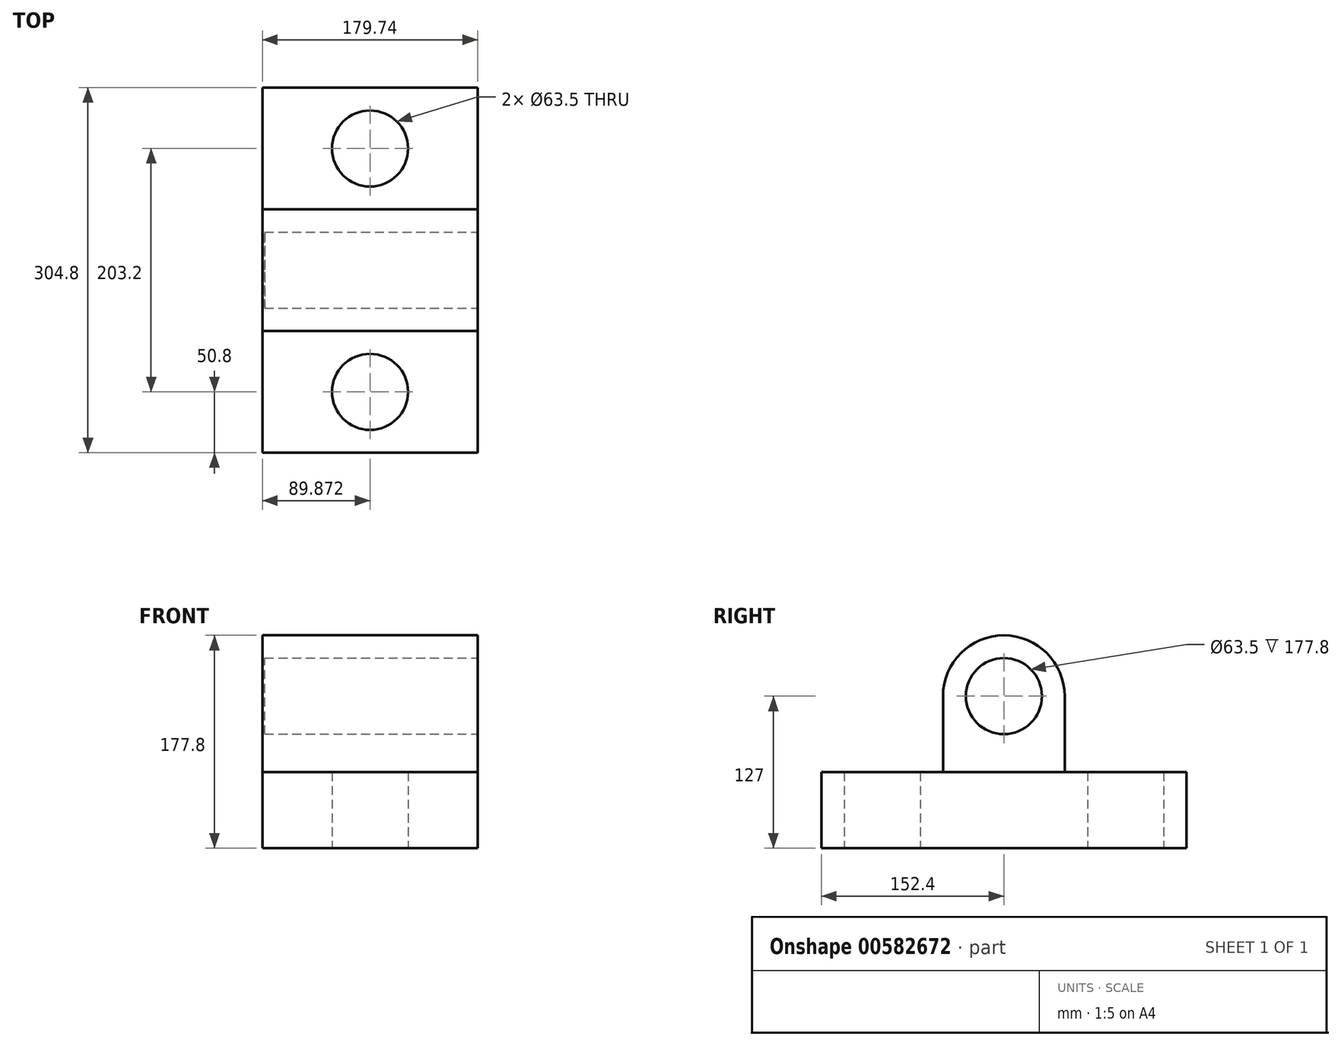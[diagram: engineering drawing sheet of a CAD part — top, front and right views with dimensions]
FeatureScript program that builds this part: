
annotation { "Feature Type Name" : "Feature", "Feature Type Description" : "" }
export const myFeature = defineFeature(function(context is Context, id is Id, definition is map)
    precondition{}
    {
        {
            var Q0;
            Q0=qCreatedBy(makeId("Top.planeOp"),FACE);
            var sketch = newSketch(context, id + "F0", { "sketchPlane" : qUnion([Q0])});
            skLineSegment(sketch, "E0.bottom", {"start": v(-43.63, 50.8) * mm, "end": v(136.11, 50.8) * mm});
            skLineSegment(sketch, "E0.top", {"start": v(-43.63, -254) * mm, "end": v(136.11, -254) * mm});
            skLineSegment(sketch, "E0.left", {"start": v(-43.63, 50.8) * mm, "end": v(-43.63, -254) * mm});
            skLineSegment(sketch, "E0.right", {"start": v(136.11, 50.8) * mm, "end": v(136.11, -254) * mm});
            skCircle(sketch, "E1", {"center": v(46.24, 0) * mm, "radius": 31.75 * mm});
            skCircle(sketch, "E2", {"center": v(46.24, -203.2) * mm, "radius": 31.75 * mm});
            skLineSegment(sketch, "E3", {"start": v(-43.63, -152.4) * mm, "end": v(136.11, -152.4) * mm});
            skPoint(sketch, "E4", {"position": v(-43.63, -50.8) * mm});
            skLineSegment(sketch, "E5", {"start": v(-43.63, -50.8) * mm, "end": v(136.11, -50.8) * mm});
            skSolve(sketch);
        }
        {
            var Q0;
            Q0 = qSketchRegion(id + "F0", true);
            extrude(context, id + "F1", {"entities" : qUnion([Q0]), "depth" : 25.4 * mm, "offsetDistance" : 25.4 * mm});
        }
        {
            var Q0;
            Q0 = qSketchRegion(id + "F0", true);
            var Q1;
            Q1=makeQuery(id+"F1.opExtrude","CAP_FACE",FACE,{"disambiguationData":[OSD([sQuery(id+"F0.wireOp",EDGE,"E0.bottom"),sQuery(id+"F0.wireOp",EDGE,"E0.top"),sQuery(id+"F0.wireOp",EDGE,"E0.left"),sQuery(id+"F0.wireOp",EDGE,"E0.right"),sQuery(id+"F0.wireOp",EDGE,"E1"),sQuery(id+"F0.wireOp",EDGE,"E2")])],"isStart":false});
            extrude(context, id + "F2", {"entities" : qUnion([Q0, Q1]), "operationType" : NewBodyOperationType.ADD, "depth" : 38.1 * mm, "offsetDistance" : 25.4 * mm});
        }
        {
            var Q0;
            {var subQ0=sQuery(id+"F0.wireOp",EDGE,"E2");var subQ1=sQuery(id+"F0.wireOp",EDGE,"E1");var subQ2=sQuery(id+"F0.wireOp",EDGE,"E0.right");var subQ3=sQuery(id+"F0.wireOp",EDGE,"E0.left");var subQ4=sQuery(id+"F0.wireOp",EDGE,"E0.top");var subQ5=sQuery(id+"F0.wireOp",EDGE,"E0.bottom");Q0=makeQuery(id+"F2.opExtrude","CAP_FACE",FACE,{"disambiguationData":[OSD([subQ5,subQ4,subQ3,subQ2,subQ1,subQ0]),TDD([makeQuery(id+"F1.opExtrude","CAP_FACE",FACE,{"disambiguationData":[OSD([subQ5,subQ4,subQ3,subQ2,subQ1,subQ0])],"isStart":false})])],"isStart":false});}
            var sketch = newSketch(context, id + "F3", { "sketchPlane" : qUnion([Q0])});
            skPoint(sketch, "E6", {"position": v(-43.63, -50.8) * mm});
            skPoint(sketch, "E7", {"position": v(-43.63, -152.4) * mm});
            skLineSegment(sketch, "E8", {"start": v(-43.63, -152.4) * mm, "end": v(136.11, -152.4) * mm});
            skLineSegment(sketch, "E9", {"start": v(-43.63, -50.8) * mm, "end": v(136.11, -50.8) * mm});
            skSolve(sketch);
        }
        {
            var Q0;
            {var subQ0=sQuery(id+"F3.wireOp",EDGE,"E8");Q0=makeQuery(id+"F3.imprint","IMPRINT",FACE,{"disambiguationData":[TD([[makeQuery(id+"F3.imprint","IMPRINT",EDGE,{"derivedFrom":subQ0}),1.0]])]});}
            extrude(context, id + "F4", {"entities" : qUnion([Q0]), "depth" : 114.3 * mm, "offsetDistance" : 25.4 * mm});
        }
        {
            var Q0;
            Q0=makeQuery(id+"F4.opExtrude","SWEPT_FACE",FACE,{"disambiguationData":[OSD([sQuery(id+"F0.wireOp",EDGE,"E0.right")])]});
            var sketch = newSketch(context, id + "F5", { "sketchPlane" : qUnion([Q0])});
            skPoint(sketch, "E10", {"position": v(-101.6, 177.8) * mm});
            skPoint(sketch, "E11", {"position": v(-152.4, 127) * mm});
            skLineSegment(sketch, "E12", {"start": v(-50.8, 127) * mm, "end": v(-50.8, 160.32) * mm});
            skPoint(sketch, "E13", {"position": v(-101.6, 127) * mm});
            skCircle(sketch, "E14", {"center": v(-101.6, 127) * mm, "radius": 31.75 * mm});
            skArc(sketch, "E15", {"start": v(-50.8, 127) * mm, "mid": v(-101.6, 177.8) * mm, "end": v(-152.4, 127) * mm});
            skSolve(sketch);
        }
        {
            var Q0;
            Q0=makeQuery(id+"F5.imprint","IMPRINT",FACE,{"disambiguationData":[TD([[makeQuery(id+"F5.imprint","IMPRINT",EDGE,{"derivedFrom":sQuery(id+"F5.wireOp",EDGE,"E14")}),1.0]])]});
            var Q1;
            {var subQ0=sQuery(id+"F5.wireOp",EDGE,"E15");var subQ1=sQuery(id+"F0.wireOp",EDGE,"E0.right");var subQ4=makeQuery(id+"F4.opExtrude","CAP_EDGE",EDGE,{"disambiguationData":[OSD([subQ1])],"isStart":false});var subQ5=makeQuery(id+"F5.imprint","INTERSECT",VERTEX,{"derivedFrom":[subQ4,subQ0]});Q1=makeQuery(id+"F5.imprint","IMPRINT",FACE,{"disambiguationData":[TD([[makeQuery(id+"F5.imprint","IMPRINT",EDGE,{"disambiguationData":[TD([[subQ5,-1.0]])],"derivedFrom":subQ0}),-1.0]])]});}
            var Q2;
            {var subQ0=sQuery(id+"F5.wireOp",EDGE,"E12");Q2=makeQuery(id+"F5.imprint","IMPRINT",FACE,{"disambiguationData":[TD([[makeQuery(id+"F5.imprint","IMPRINT",EDGE,{"derivedFrom":subQ0}),-1.0]])]});}
            extrude(context, id + "F6", {"entities" : qUnion([Q0, Q1, Q2]), "operationType" : NewBodyOperationType.REMOVE, "endBound" : BoundingType.SYMMETRIC, "oppositeDirection" : true, "depth" : 355.6 * mm, "offsetDistance" : 25.4 * mm});
        }
        {
            var Q0;
            Q0=makeQuery(id+"F6.boolean.opBoolean","COPY",FACE,{"derivedFrom":makeQuery(id+"F6.opExtrude","CAP_FACE",FACE,{"disambiguationData":[OSD([sQuery(id+"F5.wireOp",EDGE,"E14")])],"isStart":false})});
            var sketch = newSketch(context, id + "F7", { "sketchPlane" : qUnion([Q0])});
            skSolve(sketch);
        }
        {
            var Q0;
            Q0=makeQuery(id+"F6.boolean.opBoolean","COPY",FACE,{"derivedFrom":makeQuery(id+"F6.opExtrude","CAP_FACE",FACE,{"disambiguationData":[OSD([sQuery(id+"F0.wireOp",EDGE,"E0.right"),sQuery(id+"F3.wireOp",EDGE,"E8"),sQuery(id+"F5.wireOp",EDGE,"E15")])],"isStart":false})});
            var Q1;
            Q1=makeQuery(id+"F6.boolean.opBoolean","COPY",FACE,{"derivedFrom":makeQuery(id+"F6.opExtrude","CAP_FACE",FACE,{"disambiguationData":[OSD([sQuery(id+"F0.wireOp",EDGE,"E0.right"),sQuery(id+"F3.wireOp",EDGE,"E9"),sQuery(id+"F5.wireOp",EDGE,"E12"),sQuery(id+"F5.wireOp",EDGE,"E15")])],"isStart":false})});
            var Q2;
            Q2=makeQuery(id+"F7.imprint","IMPRINT",FACE,{"disambiguationData":[TD([[makeQuery(id+"F7.imprint","IMPRINT",EDGE,{"derivedFrom":makeQuery(id+"F6.boolean.opBoolean","COPY",EDGE,{"derivedFrom":makeQuery(id+"F6.opExtrude","CAP_EDGE",EDGE,{"disambiguationData":[OSD([sQuery(id+"F5.wireOp",EDGE,"E14")])],"isStart":false})})}),1.0]])]});
            extrude(context, id + "F8", {"entities" : qUnion([Q0, Q1, Q2]), "operationType" : NewBodyOperationType.REMOVE, "endBound" : BoundingType.SYMMETRIC, "oppositeDirection" : true, "depth" : 25.4 * mm, "offsetDistance" : 25.4 * mm});
        }
    });
